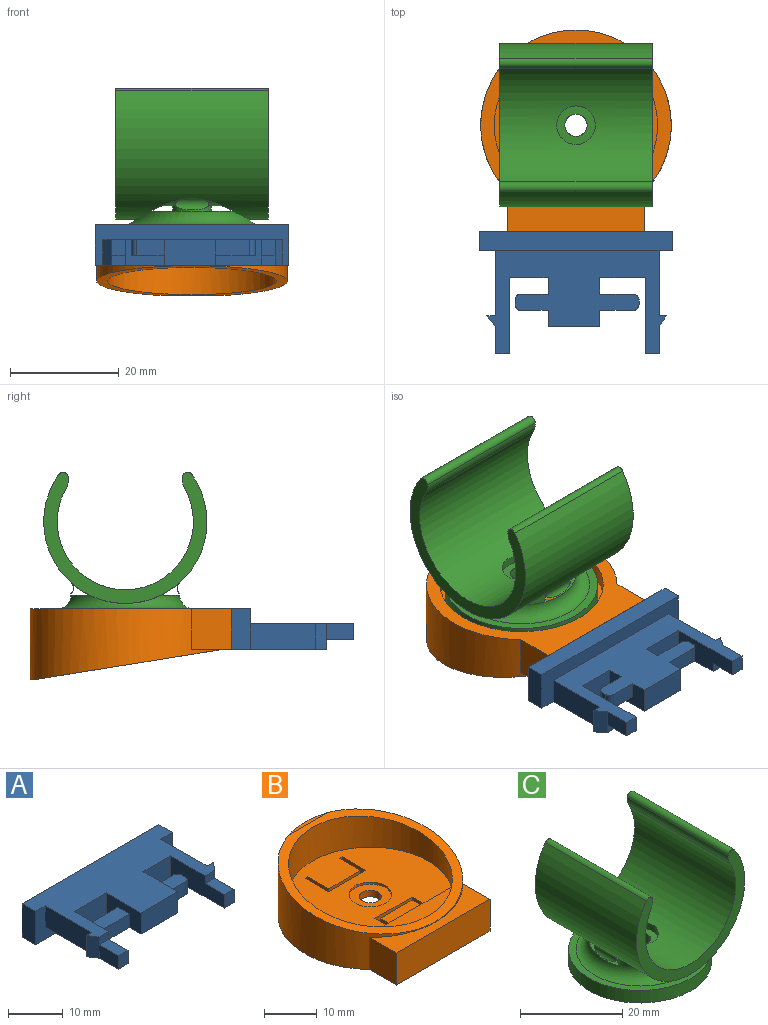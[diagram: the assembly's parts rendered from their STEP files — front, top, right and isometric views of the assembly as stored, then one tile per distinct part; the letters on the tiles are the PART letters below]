
ASSEMBLY  parts=3 mates=2
PART A: 40 faces, bbox 35.5x22.5x7.5 mm
  f0: plane 32.98x19mm, normal (0,0,-1), area 347.2mm2, adj f1,f2,f4,f5,f6,f7,f10,f13
  f1: plane 4.75x1.65mm, normal (0,1,0), area 7.8mm2, adj f0,f3,f14,f38
  f2: plane 9x4.75mm, normal (1,0,0), area 33.8mm2, adj f0,f3,f6,f16,f26,f27,f28
  f3: plane 35.5x17.5mm, normal (0,0,1), area 407.7mm2, adj f1,f2,f6,f7,f8,f9,f10,f11
  f4: plane 5x3mm, normal (1,0,0), area 15mm2, adj f0,f20,f24,f38
  f5: plane 5x3mm, normal (-1,0,0), area 15mm2, adj f0,f18,f25,f39
  f6: plane 7.12x4.75mm, normal (0,-1,0), area 33.8mm2, adj f0,f2,f3,f19
  f7: plane 8.38x4.75mm, normal (0,-1,0), area 39.8mm2, adj f0,f3,f15,f17
  f8: plane 35.5x7.5mm, normal (0,1,0), area 266.2mm2, adj f3,f9,f11,f12
  f9: plane 7.5x3.5mm, normal (-1,0,0), area 26.2mm2, adj f3,f8,f10,f12
  f10: plane 35.5x7.5mm, normal (0,-1,0), area 123.7mm2, adj f0,f3,f9,f11,f12,f13,f14
  f11: plane 7.5x3.5mm, normal (1,0,0), area 26.2mm2, adj f3,f8,f10,f12
  f12: plane 35.5x3.5mm, normal (0,0,-1), area 124.2mm2, adj f8,f9,f10,f11
  f13: plane 12x4.75mm, normal (-1,0,0), area 57mm2, adj f0,f3,f10,f22
  f14: plane 12x4.75mm, normal (1,0,0), area 57mm2, adj f0,f1,f3,f10
  f15: plane 9x4.75mm, normal (-1,0,0), area 33.8mm2, adj f0,f3,f7,f16,f30,f31,f32
  f16: plane 9.5x4.75mm, normal (0,-1,0), area 45.1mm2, adj f0,f2,f3,f15
  f17: plane 14x4.75mm, normal (1,0,0), area 57.8mm2, adj f0,f3,f7,f18,f21,f25
  f18: plane 3x2.5mm, normal (0,-1,0), area 7.5mm2, adj f0,f5,f17,f25
  f19: plane 14x4.75mm, normal (-1,0,0), area 57.8mm2, adj f0,f3,f6,f20,f23,f24
  f20: plane 3x2.5mm, normal (0,-1,0), area 7.5mm2, adj f0,f4,f19,f24
  f21: plane 2.5x1.75mm, normal (0,-1,0), area 4.4mm2, adj f3,f17,f25,f39
  f22: plane 4.75x1.33mm, normal (0,1,0), area 6.3mm2, adj f0,f3,f13,f39
  f23: plane 2.5x1.75mm, normal (0,-1,0), area 4.4mm2, adj f3,f19,f24,f38
  f24: plane 5x2.5mm, normal (0,0,1), area 12.5mm2, adj f4,f19,f20,f23
  f25: plane 5x2.5mm, normal (0,0,1), area 12.5mm2, adj f5,f17,f18,f21
  f26: plane 5.03x3mm, normal (0,-1,0), area 15.1mm2, adj f0,f2,f28,f37
  f27: plane 5.03x3mm, normal (0,1,0), area 15.1mm2, adj f0,f2,f28,f36
  f28: plane 6x3mm, normal (0,0,1), area 17.6mm2, adj f2,f26,f27,f29,f36,f37
  f29: plane 3x1.07mm, normal (1,0,0), area 3.2mm2, adj f0,f28,f36,f37
  f30: plane 6.14x3mm, normal (0,1,0), area 18.4mm2, adj f0,f15,f32,f35
  f31: plane 6.14x3mm, normal (0,-1,0), area 18.4mm2, adj f0,f15,f32,f34
  f32: plane 7.2x3mm, normal (0,0,1), area 21.1mm2, adj f15,f30,f31,f33,f34,f35
  f33: plane 3x0.88mm, normal (-1,0,0), area 2.6mm2, adj f0,f32,f34,f35
  f34: cylinder r=1.06mm len=3mm, axis (0,0,-1), area 5mm2, adj f0,f31,f32,f33
  f35: cylinder r=1.06mm len=3mm, axis (0,0,1), area 5mm2, adj f0,f30,f32,f33
  f36: cylinder r=0.97mm len=3mm, axis (0,0,-1), area 4.6mm2, adj f0,f27,f28,f29
  f37: cylinder r=0.97mm len=3mm, axis (0,0,1), area 4.6mm2, adj f0,f26,f28,f29
  f38: plane 4.75x2mm, normal (0.77,-0.64,0), area 12.3mm2, adj f0,f1,f3,f4,f23
  f39: plane 4.75x2mm, normal (-0.83,-0.55,0), area 11.4mm2, adj f0,f3,f5,f21,f22
PART B: 40 faces, bbox 35.8x37.8x13.8 mm
  f0: cylinder r=2.05mm len=4.1mm, axis (0,0,1), area 19.3mm2, adj f3,f39
  f1: plane 31x27mm, normal (0,0,1), area 578.6mm2, adj f8,f10,f11,f17,f18,f19,f20,f21
  f2: plane 8.53x4.63mm, normal (0,0,1), area 39.5mm2, adj f13,f14,f15,f27
  f3: plane 30x30mm, normal (0,0,-1), area 654.3mm2, adj f0,f9,f10,f11,f12,f13,f14,f15
  f4: cylinder r=17.5mm len=35mm, axis (0,0,-1), area 919.6mm2, adj f5,f6,f7,f30,f31,f32
  f5: plane 10.53x0.81mm, normal (0,0,1), area 5.7mm2, adj f4,f7
  f6: plane 37x35mm, normal (0,0,-1), area 346mm2, adj f4,f9,f30,f31,f33
  f7: plane 35.85x35.04mm, normal (0,-0.16,0.99), area 204.2mm2, adj f4,f5,f8
  f8: cylinder r=15.5mm len=31mm, axis (0,0,1), area 463mm2, adj f1,f7,f26,f27
  f9: cylinder r=15mm len=30mm, axis (0,0,-1), area 282.7mm2, adj f3,f6
  f10: plane 9.92x2mm, normal (0,-1,0), area 19.8mm2, adj f1,f3,f11,f17
  f11: plane 6.33x2mm, normal (1,0,0), area 12.7mm2, adj f1,f3,f10,f12,f28
  f12: plane 2x0.7mm, normal (0,1,0), area 1.4mm2, adj f3,f11,f13,f28
  f13: plane 5.64x2mm, normal (-1,0,0), area 11.3mm2, adj f2,f3,f12,f14,f28
  f14: plane 8.53x2mm, normal (0,1,0), area 17.1mm2, adj f2,f3,f13,f15
  f15: plane 5.64x2mm, normal (1,0,0), area 11.3mm2, adj f2,f3,f14,f16,f29
  f16: plane 2x0.7mm, normal (0,1,0), area 1.4mm2, adj f3,f15,f17,f29
  f17: plane 6.33x2mm, normal (-1,0,0), area 12.7mm2, adj f1,f3,f10,f16,f29
  f18: plane 6.33x2mm, normal (-1,0,0), area 12.7mm2, adj f1,f3,f19,f25
  f19: plane 2x0.7mm, normal (0,-1,0), area 1.4mm2, adj f1,f3,f18,f20
  f20: plane 5.64x2mm, normal (1,0,0), area 11.3mm2, adj f1,f3,f19,f21
  f21: plane 8.53x2mm, normal (0,-1,0), area 17.1mm2, adj f1,f3,f20,f22
  f22: plane 5.64x2mm, normal (-1,0,0), area 11.3mm2, adj f1,f3,f21,f23
  f23: plane 2x0.7mm, normal (0,-1,0), area 1.4mm2, adj f1,f3,f22,f24
  f24: plane 6.33x2mm, normal (1,0,0), area 12.7mm2, adj f1,f3,f23,f25
  f25: plane 9.92x2mm, normal (0,1,0), area 19.8mm2, adj f1,f3,f18,f24
  f26: plane 20.78x4mm, normal (0,0,1), area 57mm2, adj f8,f27
  f27: plane 20.78x2.4mm, normal (0,1,0), area 49.9mm2, adj f1,f2,f8,f26,f28,f29
  f28: plane 1.01x0.7mm, normal (0,0,-1), area 0.7mm2, adj f11,f12,f13,f27
  f29: plane 1.01x0.7mm, normal (0,0,-1), area 0.7mm2, adj f15,f16,f17,f27
  f30: plane 7.4x7.25mm, normal (1,0,0), area 53.7mm2, adj f4,f6,f32,f33
  f31: plane 7.4x7.25mm, normal (-1,0,0), area 53.7mm2, adj f4,f6,f32,f33
  f32: plane 25x7.25mm, normal (0,0,1), area 90.8mm2, adj f4,f30,f31,f33
  f33: plane 25x7.4mm, normal (0,-1,0), area 185mm2, adj f6,f30,f31,f32
  f34: plane 0.77x0.77mm, normal (0,0,-1), area 0.5mm2, adj f37
  f35: plane 0.77x0.77mm, normal (0,0,-1), area 0.5mm2, adj f36
  f36: torus R=0.38mm, axis (0,0,1), area 5.7mm2, adj f3,f35
  f37: torus R=0.38mm, axis (0,0,1), area 5.7mm2, adj f3,f34
  f38: cylinder r=4.05mm len=8.1mm, axis (0,0,1), area 12.7mm2, adj f1,f39
  f39: plane 8.1x8.1mm, normal (0,0,1), area 38.3mm2, adj f0,f38
PART C: 21 faces, bbox 30.9x30.9x28.1 mm
  f0: cylinder r=2.05mm len=4.1mm, axis (0,0,-1), area 43.8mm2, adj f18,f20
  f1: cylinder r=12.5mm len=28mm, axis (0,1,0), area 1420.4mm2, adj f9,f10,f13,f14,f17
  f2: cylinder r=10mm len=15.18mm, axis (0,0,-1), area 14.4mm2, adj f4,f8,f12
  f3: cylinder r=10mm len=15.18mm, axis (0,0,-1), area 14.4mm2, adj f4,f8,f11
  f4: torus R=12.49mm, axis (0,0,1), area 238.9mm2, adj f2,f3,f6,f8
  f5: cylinder r=14mm len=28mm, axis (0,0,-1), area 263.9mm2, adj f6,f7
  f6: plane 28x28mm, normal (0,0,1), area 125.9mm2, adj f4,f5
  f7: plane 28x28mm, normal (0,0,-1), area 557mm2, adj f5,f19
  f8: cylinder r=15mm len=30mm, axis (0,1,0), area 1493.3mm2, adj f2,f3,f4,f9,f10,f11,f12,f15
  f9: plane 30x24.07mm, normal (0,-1,0), area 153.2mm2, adj f1,f8,f13,f14,f15,f16
  f10: plane 30x24.07mm, normal (0,1,0), area 153.2mm2, adj f1,f8,f13,f14,f15,f16
  f11: cylinder r=1.3mm len=6.23mm, axis (0,1,0), area 11.3mm2, adj f3,f8
  f12: cylinder r=1.3mm len=6.23mm, axis (0,1,0), area 11.3mm2, adj f2,f8
  f13: cylinder r=3.44mm len=28mm, axis (0,1,0), area 58.1mm2, adj f1,f9,f10,f15
  f14: cylinder r=3.44mm len=28mm, axis (0,-1,0), area 58.1mm2, adj f1,f9,f10,f16
  f15: cylinder r=1mm len=28mm, axis (0,1,0), area 68.3mm2, adj f8,f9,f10,f13
  f16: cylinder r=1mm len=28mm, axis (0,-1,0), area 68.3mm2, adj f8,f9,f10,f14
  f17: cylinder r=3.55mm len=7.1mm, axis (0,0,1), area 28mm2, adj f1,f18
  f18: plane 7.1x7.1mm, normal (0,0,1), area 26.4mm2, adj f0,f17
  f19: cylinder r=4.33mm len=8.65mm, axis (0,0,-1), area 57.1mm2, adj f7,f20
  f20: plane 8.65x8.65mm, normal (0,0,-1), area 45.6mm2, adj f0,f19
PLACE A rot(axis=(0,-1,0),180deg) t=(-1.65,20.12,6.08)mm
PLACE B rot(axis=(0,-1,0),180deg) t=(-1.65,22.12,6.03)mm
PLACE C rot(axis=(0,0,-1),90deg) t=(-1.65,22.12,3.03)mm
MATE revolute B.f0 <-> C.f5  axis (0,0,1) through (-1.65,22.12,3.03)mm
MATE fastened B.f33 <-> A.f8  axis (0,-1,0) through (-1.65,2.62,2.33)mm
